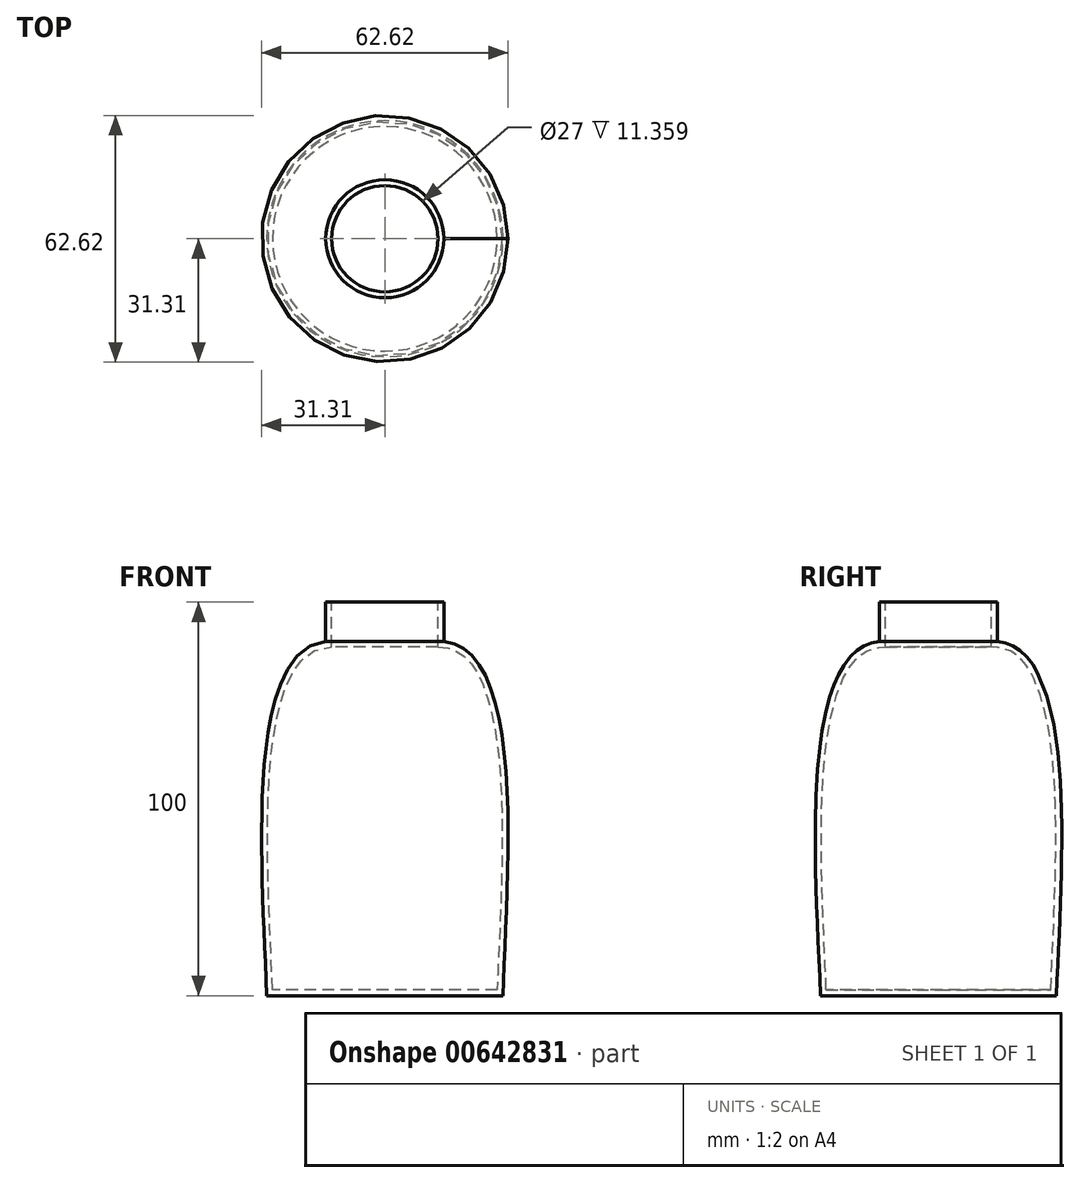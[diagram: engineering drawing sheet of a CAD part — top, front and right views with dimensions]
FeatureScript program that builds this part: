
annotation { "Feature Type Name" : "Feature", "Feature Type Description" : "" }
export const myFeature = defineFeature(function(context is Context, id is Id, definition is map)
    precondition{}
    {
        {
            var Q0;
            Q0=qCreatedBy(makeId("Front.planeOp"),FACE);
            var sketch = newSketch(context, id + "F0", { "sketchPlane" : qUnion([Q0])});
            skLineSegment(sketch, "E0", {"start": v(0, 50) * mm, "end": v(0, -50) * mm});
            skLineSegment(sketch, "E1", {"start": v(0, 50) * mm, "end": v(-15, 50) * mm});
            skLineSegment(sketch, "E2", {"start": v(0, -50) * mm, "end": v(-30, -50) * mm});
            skLineSegment(sketch, "E3", {"start": v(-15, 50) * mm, "end": v(-15, 40) * mm});
            skFitSpline(sketch, "E4", {"points": [v(-15, 40) * mm, v(-30, -50) * mm], "startDerivative": vector(-64.93, -6.42) * mm, "endDerivative": vector(2.41, -82.81) * mm});
            skLineSegment(sketch, "E5", {"start": v(0, 64.14) * mm, "end": v(0, -59.3) * mm, "construction": true});
            skSolve(sketch);
        }
        {
            var Q0;
            Q0=makeQuery(id+"F0.imprint","IMPRINT",FACE,{"disambiguationData":[TD([[makeQuery(id+"F0.imprint","IMPRINT",EDGE,{"derivedFrom":sQuery(id+"F0.wireOp",EDGE,"E0")}),-1.0]])]});
            var Q1;
            Q1=sQuery(id+"F0.wireOp",EDGE,"E5");
            revolve(context, id + "F1", {"entities" : qUnion([Q0]), "axis" : qUnion([Q1]), "revolveType" : RevolveType.FULL});
        }
        {
            var Q0;
            Q0=makeQuery(id+"F1.opRevolve","SWEPT_FACE",FACE,{"disambiguationData":[OSD([sQuery(id+"F0.wireOp",EDGE,"E1")])]});
            shell(context, id + "F2", {"entities" : qUnion([Q0]), "thickness" : 1.5 * mm});
        }
    });
